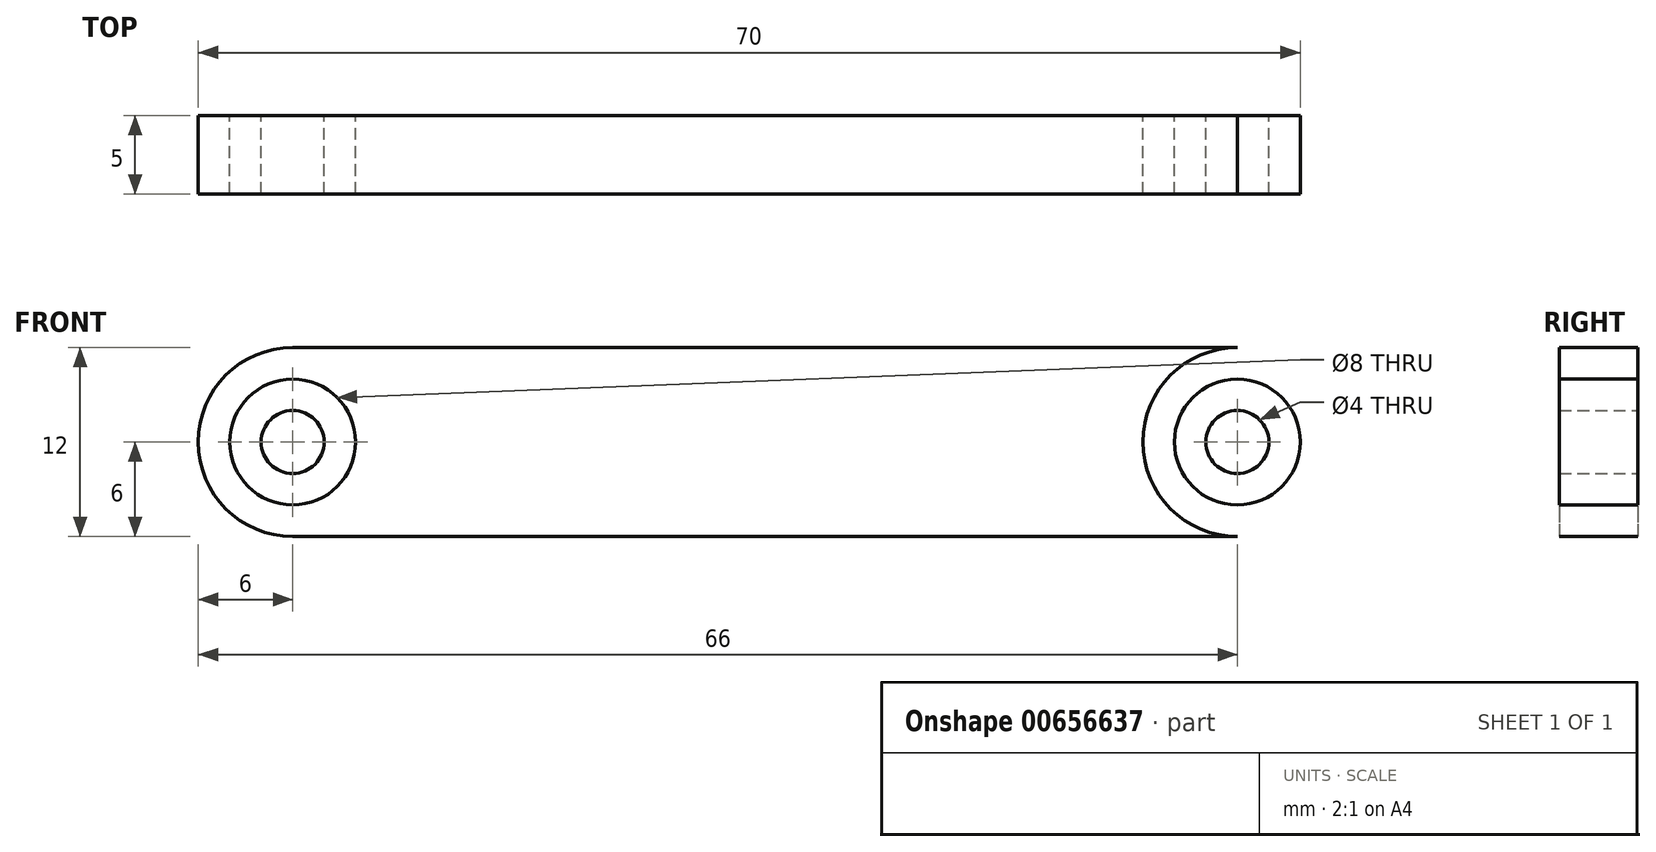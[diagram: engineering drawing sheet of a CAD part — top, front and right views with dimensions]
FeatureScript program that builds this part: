
annotation { "Feature Type Name" : "Feature", "Feature Type Description" : "" }
export const myFeature = defineFeature(function(context is Context, id is Id, definition is map)
    precondition{}
    {
        {
            var Q0;
            Q0=qCreatedBy(makeId("Front.planeOp"),FACE);
            var sketch = newSketch(context, id + "F0", { "sketchPlane" : qUnion([Q0])});
            skCircle(sketch, "E0", {"center": v(-30, 0) * mm, "radius": 2 * mm});
            skCircle(sketch, "E1", {"center": v(-30, 0) * mm, "radius": 4 * mm});
            skCircle(sketch, "E2", {"center": v(-30, 0) * mm, "radius": 6 * mm});
            skLineSegment(sketch, "E3", {"start": v(-30, 6) * mm, "end": v(0, 6) * mm});
            skLineSegment(sketch, "E4", {"start": v(-30, -6) * mm, "end": v(0, -6) * mm});
            skCircle(sketch, "E5.MirrorC", {"center": v(30, 0) * mm, "radius": 2 * mm});
            skCircle(sketch, "E6.MirrorC", {"center": v(30, 0) * mm, "radius": 4 * mm});
            skCircle(sketch, "E7.MirrorC", {"center": v(30, 0) * mm, "radius": 6 * mm});
            skLineSegment(sketch, "E8.MirrorCS", {"start": v(30, 6) * mm, "end": v(0, 6) * mm});
            skLineSegment(sketch, "E9.MirrorCS", {"start": v(30, -6) * mm, "end": v(0, -6) * mm});
            skSolve(sketch);
        }
        {
            var Q0;
            {var subQ4=sQuery(id+"F0.wireOp",EDGE,"E3");Q0=makeQuery(id+"F0.imprint","IMPRINT",FACE,{"disambiguationData":[TD([[makeQuery(id+"F0.imprint","IMPRINT",EDGE,{"derivedFrom":subQ4}),-1.0]])]});}
            var Q1;
            Q1=makeQuery(id+"F0.imprint","IMPRINT",FACE,{"disambiguationData":[TD([[makeQuery(id+"F0.imprint","IMPRINT",EDGE,{"derivedFrom":sQuery(id+"F0.wireOp",EDGE,"E1")}),-1.0]])]});
            var Q2;
            Q2=makeQuery(id+"F0.imprint","IMPRINT",FACE,{"disambiguationData":[TD([[makeQuery(id+"F0.imprint","IMPRINT",EDGE,{"derivedFrom":sQuery(id+"F0.wireOp",EDGE,"E0")}),1.0]])]});
            var Q3;
            Q3=makeQuery(id+"F0.imprint","IMPRINT",FACE,{"disambiguationData":[TD([[makeQuery(id+"F0.imprint","IMPRINT",EDGE,{"derivedFrom":sQuery(id+"F0.wireOp",EDGE,"E5.MirrorC")}),-1.0]])]});
            var Q4;
            Q4=makeQuery(id+"F0.imprint","IMPRINT",FACE,{"disambiguationData":[TD([[makeQuery(id+"F0.imprint","IMPRINT",EDGE,{"derivedFrom":sQuery(id+"F0.wireOp",EDGE,"E6.MirrorC")}),1.0]])]});
            extrude(context, id + "F1", {"entities" : qUnion([Q0, Q1, Q2, Q3, Q4]), "depth" : 5 * mm, "offsetDistance" : 25 * mm});
        }
    });
